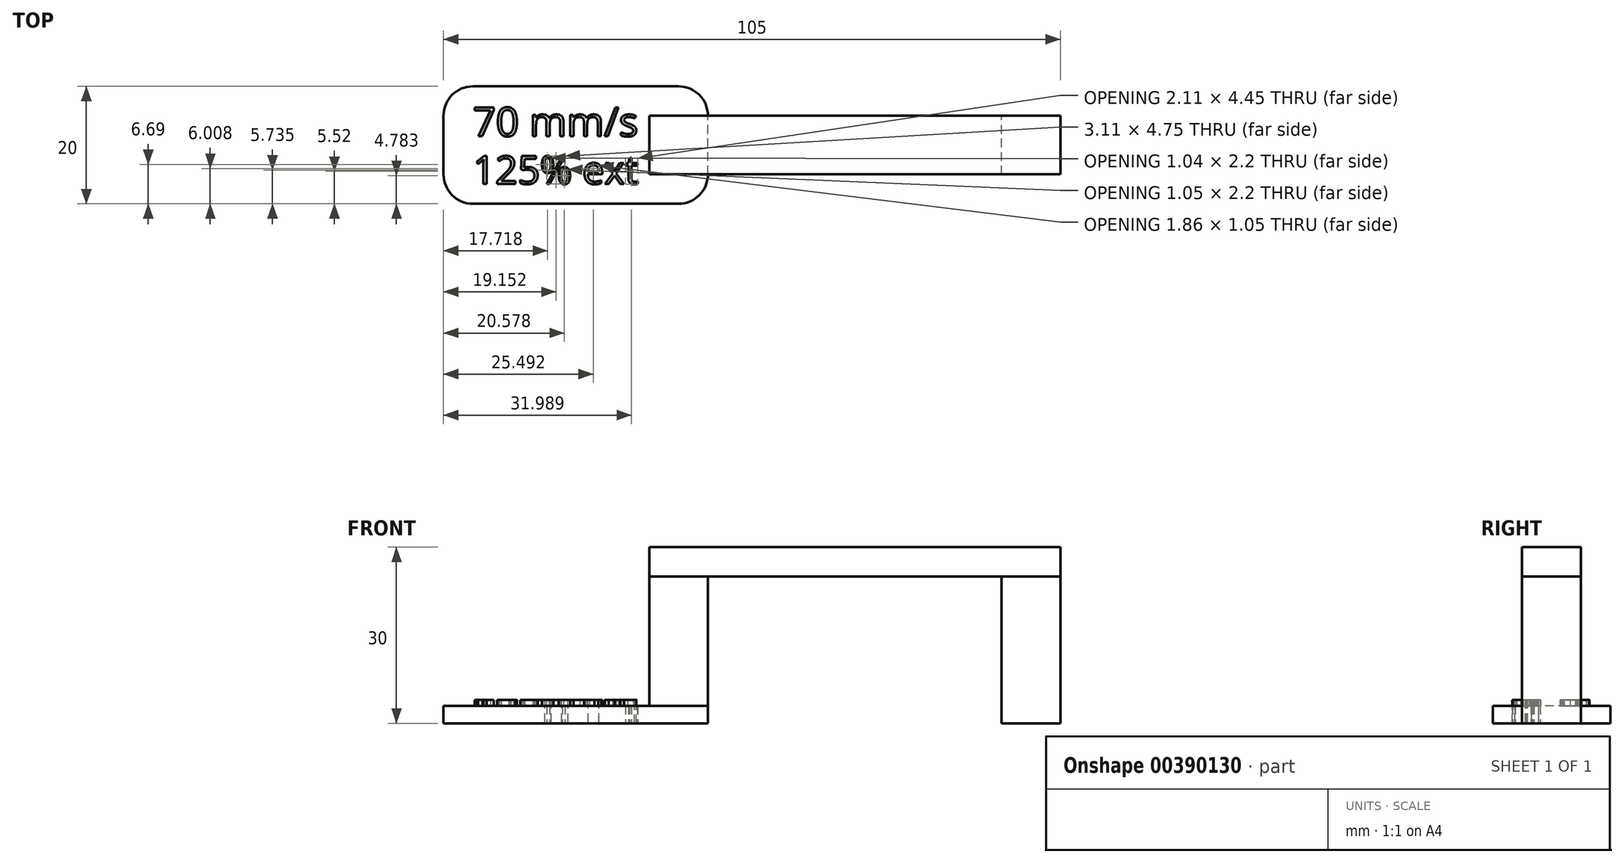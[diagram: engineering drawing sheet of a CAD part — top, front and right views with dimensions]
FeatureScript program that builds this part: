
annotation { "Feature Type Name" : "Feature", "Feature Type Description" : "" }
export const myFeature = defineFeature(function(context is Context, id is Id, definition is map)
    precondition{}
    {
        {
            var Q0;
            Q0=qCreatedBy(makeId("Top.planeOp"),FACE);
            var sketch = newSketch(context, id + "F0", { "sketchPlane" : qUnion([Q0])});
            skLineSegment(sketch, "E0.bottom", {"start": v(-25, -5) * mm, "end": v(25, -5) * mm});
            skLineSegment(sketch, "E0.top", {"start": v(-25, 5) * mm, "end": v(25, 5) * mm});
            skLineSegment(sketch, "E0.left", {"start": v(-25, -5) * mm, "end": v(-25, 5) * mm});
            skLineSegment(sketch, "E0.right", {"start": v(25, -5) * mm, "end": v(25, 5) * mm});
            skLineSegment(sketch, "E1.bottom", {"start": v(25, -5) * mm, "end": v(35, -5) * mm});
            skLineSegment(sketch, "E1.top", {"start": v(25, 5) * mm, "end": v(35, 5) * mm});
            skLineSegment(sketch, "E1.right", {"start": v(35, -5) * mm, "end": v(35, 5) * mm});
            skPoint(sketch, "E2.oppositeSnap0", {"position": v(0, -5) * mm});
            skLineSegment(sketch, "E2.bottom", {"start": v(-25, 5) * mm, "end": v(-35, 5) * mm});
            skLineSegment(sketch, "E2.top", {"start": v(-25, -5) * mm, "end": v(-35, -5) * mm});
            skLineSegment(sketch, "E2.left", {"start": v(-25, 5) * mm, "end": v(-25, -5) * mm});
            skLineSegment(sketch, "E2.right", {"start": v(-35, 5) * mm, "end": v(-35, -5) * mm});
            skLineSegment(sketch, "E3", {"start": v(-25, 5) * mm, "end": v(-25, 5) * mm});
            skLineSegment(sketch, "E4", {"start": v(-30, 10) * mm, "end": v(-65, 10) * mm});
            skLineSegment(sketch, "E5", {"start": v(-70, 5) * mm, "end": v(-70, -5) * mm});
            skLineSegment(sketch, "E6", {"start": v(-65, -10) * mm, "end": v(-30, -10) * mm});
            skLineSegment(sketch, "E7", {"start": v(-25, -5) * mm, "end": v(-25, -5) * mm});
            skLineSegment(sketch, "E8", {"start": v(-35, 0) * mm, "end": v(25, 0) * mm, "construction": true});
            skPoint(sketch, "E9.visualSharp", {"position": v(-70, -10) * mm});
            skArc(sketch, "E9.filletArc", {"start": v(-70, -5) * mm, "mid": v(-68.54, -8.54) * mm, "end": v(-65, -10) * mm});
            skPoint(sketch, "E10.visualSharp", {"position": v(-70, 10) * mm});
            skArc(sketch, "E10.filletArc", {"start": v(-65, 10) * mm, "mid": v(-68.54, 8.54) * mm, "end": v(-70, 5) * mm});
            skPoint(sketch, "E11.visualSharp", {"position": v(-25, -10) * mm});
            skArc(sketch, "E11.filletArc", {"start": v(-30, -10) * mm, "mid": v(-26.46, -8.54) * mm, "end": v(-25, -5) * mm});
            skPoint(sketch, "E12.visualSharp", {"position": v(-25, 10) * mm});
            skArc(sketch, "E12.filletArc", {"start": v(-25, 5) * mm, "mid": v(-26.46, 8.54) * mm, "end": v(-30, 10) * mm});
            skText(sketch, "E13", { "text": "70 mm/s", "fontName": "OpenSans-Regular.ttf"});
            skText(sketch, "E14", { "text": "125% ext", "fontName": "OpenSans-Regular.ttf"});
            const initialGuessF0  = {"E13": [-0.065, 0.00149, 1, 0, 0.00493], "E14": [-0.065, -0.00664, 1, 0, 0.00479]};
            skSetInitialGuess(sketch, initialGuessF0);
            skSolve(sketch);
        }
        {
            var Q0;
            Q0=makeQuery(id+"F0.imprint","IMPRINT",FACE,{"disambiguationData":[TD([[makeQuery(id+"F0.imprint","IMPRINT",EDGE,{"derivedFrom":sQuery(id+"F0.wireOp",EDGE,"E1.bottom")}),1.0]])]});
            var Q1;
            Q1=makeQuery(id+"F0.imprint","IMPRINT",FACE,{"disambiguationData":[TD([[makeQuery(id+"F0.imprint","IMPRINT",EDGE,{"derivedFrom":sQuery(id+"F0.wireOp",EDGE,"E2.bottom")}),1.0]])]});
            extrude(context, id + "F1", {"entities" : qUnion([Q0, Q1]), "depth" : 25 * mm});
        }
        {
            var Q0;
            Q0=makeQuery(id+"F0.imprint","IMPRINT",FACE,{"disambiguationData":[TD([[makeQuery(id+"F0.imprint","IMPRINT",EDGE,{"derivedFrom":sQuery(id+"F0.wireOp",EDGE,"E0.bottom")}),1.0]])]});
            var Q1;
            Q1=makeQuery(id+"F0.imprint","IMPRINT",FACE,{"disambiguationData":[TD([[makeQuery(id+"F0.imprint","IMPRINT",EDGE,{"derivedFrom":sQuery(id+"F0.wireOp",EDGE,"E2.bottom")}),1.0]])]});
            var Q2;
            Q2=makeQuery(id+"F0.imprint","IMPRINT",FACE,{"disambiguationData":[TD([[makeQuery(id+"F0.imprint","IMPRINT",EDGE,{"derivedFrom":sQuery(id+"F0.wireOp",EDGE,"E1.bottom")}),1.0]])]});
            var Q3;
            Q3=makeQuery(id+"F1.opExtrude","CAP_FACE",FACE,{"disambiguationData":[OSD([sQuery(id+"F0.wireOp",EDGE,"E1.bottom"),sQuery(id+"F0.wireOp",EDGE,"E1.top"),sQuery(id+"F0.wireOp",EDGE,"E0.right"),sQuery(id+"F0.wireOp",EDGE,"E1.right")])],"isStart":false});
            extrude(context, id + "F2", {"entities" : qUnion([Q0, Q1, Q2]), "depth" : 30 * mm, "hasSecondDirection" : true, "secondDirectionBound" : SecondDirectionBoundingType.UP_TO_SURFACE, "secondDirectionOppositeDirection" : false, "secondDirectionBoundEntityFace" : qUnion([Q3]), "secondDirectionDepth" : 25 * mm});
        }
        {
            var Q0;
            Q0=makeQuery(id+"F0.imprint","IMPRINT",FACE,{"disambiguationData":[TD([[makeQuery(id+"F0.imprint","IMPRINT",EDGE,{"derivedFrom":sQuery(id+"F0.wireOp",EDGE,"E2.bottom")}),1.0]])]});
            var Q1;
            Q1=makeQuery(id+"F0.imprint","IMPRINT",FACE,{"disambiguationData":[TD([[makeQuery(id+"F0.imprint","IMPRINT",EDGE,{"derivedFrom":sQuery(id+"F0.wireOp",EDGE,"E2.bottom")}),-1.0]])]});
            var Q2;
            Q2=makeQuery(id+"F0.imprint","IMPRINT",FACE,{"disambiguationData":[TD([[makeQuery(id+"F0.imprint","IMPRINT",EDGE,{"derivedFrom":sQuery(id+"F0.wireOp",EDGE,"E13.sketch_text.stroke-0")}),-1.0]])]});
            var Q3;
            Q3=makeQuery(id+"F0.imprint","IMPRINT",FACE,{"disambiguationData":[TD([[makeQuery(id+"F0.imprint","IMPRINT",EDGE,{"derivedFrom":sQuery(id+"F0.wireOp",EDGE,"E13.sketch_text.stroke-36")}),1.0]])]});
            var Q4;
            Q4=makeQuery(id+"F0.imprint","IMPRINT",FACE,{"disambiguationData":[TD([[makeQuery(id+"F0.imprint","IMPRINT",EDGE,{"derivedFrom":sQuery(id+"F0.wireOp",EDGE,"E13.sketch_text.stroke-28")}),-1.0]])]});
            var Q5;
            Q5=makeQuery(id+"F0.imprint","IMPRINT",FACE,{"disambiguationData":[TD([[makeQuery(id+"F0.imprint","IMPRINT",EDGE,{"derivedFrom":sQuery(id+"F0.wireOp",EDGE,"E14.sketch_text.stroke-89")}),1.0]])]});
            var Q6;
            Q6=makeQuery(id+"F0.imprint","IMPRINT",FACE,{"disambiguationData":[TD([[makeQuery(id+"F0.imprint","IMPRINT",EDGE,{"derivedFrom":sQuery(id+"F0.wireOp",EDGE,"E14.sketch_text.stroke-55")}),-1.0]])]});
            var Q7;
            Q7=makeQuery(id+"F0.imprint","IMPRINT",FACE,{"disambiguationData":[TD([[makeQuery(id+"F0.imprint","IMPRINT",EDGE,{"derivedFrom":sQuery(id+"F0.wireOp",EDGE,"E14.sketch_text.stroke-94")}),-1.0]])]});
            var Q8;
            Q8=makeQuery(id+"F0.imprint","IMPRINT",FACE,{"disambiguationData":[TD([[makeQuery(id+"F0.imprint","IMPRINT",EDGE,{"derivedFrom":sQuery(id+"F0.wireOp",EDGE,"E14.sketch_text.stroke-41")}),-1.0]])]});
            var Q9;
            Q9=makeQuery(id+"F0.imprint","IMPRINT",FACE,{"disambiguationData":[TD([[makeQuery(id+"F0.imprint","IMPRINT",EDGE,{"derivedFrom":sQuery(id+"F0.wireOp",EDGE,"E14.sketch_text.stroke-25")}),-1.0]])]});
            var Q10;
            Q10=makeQuery(id+"F0.imprint","IMPRINT",FACE,{"disambiguationData":[TD([[makeQuery(id+"F0.imprint","IMPRINT",EDGE,{"derivedFrom":sQuery(id+"F0.wireOp",EDGE,"E14.sketch_text.stroke-9")}),-1.0]])]});
            var Q11;
            Q11=makeQuery(id+"F0.imprint","IMPRINT",FACE,{"disambiguationData":[TD([[makeQuery(id+"F0.imprint","IMPRINT",EDGE,{"derivedFrom":sQuery(id+"F0.wireOp",EDGE,"E14.sketch_text.stroke-106")}),-1.0]])]});
            var Q12;
            Q12=makeQuery(id+"F0.imprint","IMPRINT",FACE,{"disambiguationData":[TD([[makeQuery(id+"F0.imprint","IMPRINT",EDGE,{"derivedFrom":sQuery(id+"F0.wireOp",EDGE,"E13.sketch_text.stroke-44")}),-1.0]])]});
            var Q13;
            Q13=makeQuery(id+"F0.imprint","IMPRINT",FACE,{"disambiguationData":[TD([[makeQuery(id+"F0.imprint","IMPRINT",EDGE,{"derivedFrom":sQuery(id+"F0.wireOp",EDGE,"E13.sketch_text.stroke-72")}),-1.0]])]});
            var Q14;
            Q14=makeQuery(id+"F0.imprint","IMPRINT",FACE,{"disambiguationData":[TD([[makeQuery(id+"F0.imprint","IMPRINT",EDGE,{"derivedFrom":sQuery(id+"F0.wireOp",EDGE,"E13.sketch_text.stroke-100")}),-1.0]])]});
            var Q15;
            Q15=makeQuery(id+"F0.imprint","IMPRINT",FACE,{"disambiguationData":[TD([[makeQuery(id+"F0.imprint","IMPRINT",EDGE,{"derivedFrom":sQuery(id+"F0.wireOp",EDGE,"E13.sketch_text.stroke-104")}),-1.0]])]});
            var Q16;
            Q16=makeQuery(id+"F0.imprint","IMPRINT",FACE,{"disambiguationData":[TD([[makeQuery(id+"F0.imprint","IMPRINT",EDGE,{"derivedFrom":sQuery(id+"F0.wireOp",EDGE,"E14.sketch_text.stroke-0")}),-1.0]])]});
            var Q17;
            Q17=makeQuery(id+"F0.imprint","IMPRINT",FACE,{"disambiguationData":[TD([[makeQuery(id+"F0.imprint","IMPRINT",EDGE,{"derivedFrom":sQuery(id+"F0.wireOp",EDGE,"E14.sketch_text.stroke-17")}),1.0]])]});
            var Q18;
            Q18=makeQuery(id+"F0.imprint","IMPRINT",FACE,{"disambiguationData":[TD([[makeQuery(id+"F0.imprint","IMPRINT",EDGE,{"derivedFrom":sQuery(id+"F0.wireOp",EDGE,"E14.sketch_text.stroke-33")}),1.0]])]});
            var Q19;
            Q19=makeQuery(id+"F0.imprint","IMPRINT",FACE,{"disambiguationData":[TD([[makeQuery(id+"F0.imprint","IMPRINT",EDGE,{"derivedFrom":sQuery(id+"F0.wireOp",EDGE,"E14.sketch_text.stroke-41")}),1.0]])]});
            var Q20;
            Q20=makeQuery(id+"F0.imprint","IMPRINT",FACE,{"disambiguationData":[TD([[makeQuery(id+"F0.imprint","IMPRINT",EDGE,{"derivedFrom":sQuery(id+"F0.wireOp",EDGE,"E14.sketch_text.stroke-55")}),1.0]])]});
            var Q21;
            Q21=makeQuery(id+"F0.imprint","IMPRINT",FACE,{"disambiguationData":[TD([[makeQuery(id+"F0.imprint","IMPRINT",EDGE,{"derivedFrom":sQuery(id+"F0.wireOp",EDGE,"E14.sketch_text.stroke-71")}),-1.0]])]});
            var Q22;
            Q22=makeQuery(id+"F0.imprint","IMPRINT",FACE,{"disambiguationData":[TD([[makeQuery(id+"F0.imprint","IMPRINT",EDGE,{"derivedFrom":sQuery(id+"F0.wireOp",EDGE,"E14.sketch_text.stroke-75")}),-1.0]])]});
            var Q23;
            Q23=makeQuery(id+"F0.imprint","IMPRINT",FACE,{"disambiguationData":[TD([[makeQuery(id+"F0.imprint","IMPRINT",EDGE,{"derivedFrom":sQuery(id+"F0.wireOp",EDGE,"E13.sketch_text.stroke-27")}),1.0]])]});
            var Q24;
            Q24=makeQuery(id+"F0.imprint","IMPRINT",FACE,{"disambiguationData":[TD([[makeQuery(id+"F0.imprint","IMPRINT",EDGE,{"derivedFrom":sQuery(id+"F0.wireOp",EDGE,"E13.sketch_text.stroke-91")}),-1.0]])]});
            var Q25;
            Q25=makeQuery(id+"F0.imprint","IMPRINT",FACE,{"disambiguationData":[TD([[makeQuery(id+"F0.imprint","IMPRINT",EDGE,{"derivedFrom":sQuery(id+"F0.wireOp",EDGE,"E13.sketch_text.stroke-15")}),1.0]])]});
            var Q26;
            Q26=makeQuery(id+"F0.imprint","IMPRINT",FACE,{"disambiguationData":[TD([[makeQuery(id+"F0.imprint","IMPRINT",EDGE,{"derivedFrom":sQuery(id+"F0.wireOp",EDGE,"E13.sketch_text.stroke-7")}),-1.0]])]});
            var Q27;
            Q27=makeQuery(id+"F0.imprint","IMPRINT",FACE,{"disambiguationData":[TD([[makeQuery(id+"F0.imprint","IMPRINT",EDGE,{"derivedFrom":sQuery(id+"F0.wireOp",EDGE,"E13.sketch_text.stroke-79")}),-1.0]])]});
            var Q28;
            Q28=makeQuery(id+"F0.imprint","IMPRINT",FACE,{"disambiguationData":[TD([[makeQuery(id+"F0.imprint","IMPRINT",EDGE,{"derivedFrom":sQuery(id+"F0.wireOp",EDGE,"E13.sketch_text.stroke-17")}),1.0]])]});
            var Q29;
            Q29=makeQuery(id+"F0.imprint","IMPRINT",FACE,{"disambiguationData":[TD([[makeQuery(id+"F0.imprint","IMPRINT",EDGE,{"derivedFrom":sQuery(id+"F0.wireOp",EDGE,"E13.sketch_text.stroke-9")}),-1.0]])]});
            var Q30;
            Q30=makeQuery(id+"F0.imprint","IMPRINT",FACE,{"disambiguationData":[TD([[makeQuery(id+"F0.imprint","IMPRINT",EDGE,{"derivedFrom":sQuery(id+"F0.wireOp",EDGE,"E13.sketch_text.stroke-81")}),-1.0]])]});
            extrude(context, id + "F3", {"entities" : qUnion([Q0, Q1, Q2, Q3, Q4, Q5, Q6, Q7, Q8, Q9, Q10, Q11, Q12, Q13, Q14, Q15, Q16, Q17, Q18, Q19, Q20, Q21, Q22, Q23, Q24, Q25, Q26, Q27, Q28, Q29, Q30]), "operationType" : NewBodyOperationType.ADD, "depth" : 3 * mm});
        }
        {
            var Q0;
            Q0=makeQuery(id+"F0.imprint","IMPRINT",FACE,{"disambiguationData":[TD([[makeQuery(id+"F0.imprint","IMPRINT",EDGE,{"derivedFrom":sQuery(id+"F0.wireOp",EDGE,"E14.sketch_text.stroke-0")}),-1.0]])]});
            var Q1;
            Q1=makeQuery(id+"F0.imprint","IMPRINT",FACE,{"disambiguationData":[TD([[makeQuery(id+"F0.imprint","IMPRINT",EDGE,{"derivedFrom":sQuery(id+"F0.wireOp",EDGE,"E14.sketch_text.stroke-9")}),-1.0]])]});
            var Q2;
            Q2=makeQuery(id+"F0.imprint","IMPRINT",FACE,{"disambiguationData":[TD([[makeQuery(id+"F0.imprint","IMPRINT",EDGE,{"derivedFrom":sQuery(id+"F0.wireOp",EDGE,"E14.sketch_text.stroke-25")}),-1.0]])]});
            var Q3;
            Q3=makeQuery(id+"F0.imprint","IMPRINT",FACE,{"disambiguationData":[TD([[makeQuery(id+"F0.imprint","IMPRINT",EDGE,{"derivedFrom":sQuery(id+"F0.wireOp",EDGE,"E14.sketch_text.stroke-41")}),-1.0]])]});
            var Q4;
            Q4=makeQuery(id+"F0.imprint","IMPRINT",FACE,{"disambiguationData":[TD([[makeQuery(id+"F0.imprint","IMPRINT",EDGE,{"derivedFrom":sQuery(id+"F0.wireOp",EDGE,"E14.sketch_text.stroke-71")}),-1.0]])]});
            var Q5;
            Q5=makeQuery(id+"F0.imprint","IMPRINT",FACE,{"disambiguationData":[TD([[makeQuery(id+"F0.imprint","IMPRINT",EDGE,{"derivedFrom":sQuery(id+"F0.wireOp",EDGE,"E14.sketch_text.stroke-55")}),-1.0]])]});
            var Q6;
            Q6=makeQuery(id+"F0.imprint","IMPRINT",FACE,{"disambiguationData":[TD([[makeQuery(id+"F0.imprint","IMPRINT",EDGE,{"derivedFrom":sQuery(id+"F0.wireOp",EDGE,"E14.sketch_text.stroke-75")}),-1.0]])]});
            var Q7;
            Q7=makeQuery(id+"F0.imprint","IMPRINT",FACE,{"disambiguationData":[TD([[makeQuery(id+"F0.imprint","IMPRINT",EDGE,{"derivedFrom":sQuery(id+"F0.wireOp",EDGE,"E14.sketch_text.stroke-94")}),-1.0]])]});
            var Q8;
            Q8=makeQuery(id+"F0.imprint","IMPRINT",FACE,{"disambiguationData":[TD([[makeQuery(id+"F0.imprint","IMPRINT",EDGE,{"derivedFrom":sQuery(id+"F0.wireOp",EDGE,"E14.sketch_text.stroke-106")}),-1.0]])]});
            var Q9;
            Q9=makeQuery(id+"F0.imprint","IMPRINT",FACE,{"disambiguationData":[TD([[makeQuery(id+"F0.imprint","IMPRINT",EDGE,{"derivedFrom":sQuery(id+"F0.wireOp",EDGE,"E13.sketch_text.stroke-28")}),-1.0]])]});
            var Q10;
            Q10=makeQuery(id+"F0.imprint","IMPRINT",FACE,{"disambiguationData":[TD([[makeQuery(id+"F0.imprint","IMPRINT",EDGE,{"derivedFrom":sQuery(id+"F0.wireOp",EDGE,"E13.sketch_text.stroke-0")}),-1.0]])]});
            var Q11;
            Q11=makeQuery(id+"F0.imprint","IMPRINT",FACE,{"disambiguationData":[TD([[makeQuery(id+"F0.imprint","IMPRINT",EDGE,{"derivedFrom":sQuery(id+"F0.wireOp",EDGE,"E13.sketch_text.stroke-44")}),-1.0]])]});
            var Q12;
            Q12=makeQuery(id+"F0.imprint","IMPRINT",FACE,{"disambiguationData":[TD([[makeQuery(id+"F0.imprint","IMPRINT",EDGE,{"derivedFrom":sQuery(id+"F0.wireOp",EDGE,"E13.sketch_text.stroke-72")}),-1.0]])]});
            var Q13;
            Q13=makeQuery(id+"F0.imprint","IMPRINT",FACE,{"disambiguationData":[TD([[makeQuery(id+"F0.imprint","IMPRINT",EDGE,{"derivedFrom":sQuery(id+"F0.wireOp",EDGE,"E13.sketch_text.stroke-100")}),-1.0]])]});
            var Q14;
            Q14=makeQuery(id+"F0.imprint","IMPRINT",FACE,{"disambiguationData":[TD([[makeQuery(id+"F0.imprint","IMPRINT",EDGE,{"derivedFrom":sQuery(id+"F0.wireOp",EDGE,"E13.sketch_text.stroke-104")}),-1.0]])]});
            var Q15;
            Q15=makeQuery(id+"F0.imprint","IMPRINT",FACE,{"disambiguationData":[TD([[makeQuery(id+"F0.imprint","IMPRINT",EDGE,{"derivedFrom":sQuery(id+"F0.wireOp",EDGE,"E13.sketch_text.stroke-91")}),-1.0]])]});
            var Q16;
            Q16=makeQuery(id+"F0.imprint","IMPRINT",FACE,{"disambiguationData":[TD([[makeQuery(id+"F0.imprint","IMPRINT",EDGE,{"derivedFrom":sQuery(id+"F0.wireOp",EDGE,"E13.sketch_text.stroke-7")}),-1.0]])]});
            var Q17;
            Q17=makeQuery(id+"F0.imprint","IMPRINT",FACE,{"disambiguationData":[TD([[makeQuery(id+"F0.imprint","IMPRINT",EDGE,{"derivedFrom":sQuery(id+"F0.wireOp",EDGE,"E13.sketch_text.stroke-79")}),-1.0]])]});
            var Q18;
            Q18=makeQuery(id+"F0.imprint","IMPRINT",FACE,{"disambiguationData":[TD([[makeQuery(id+"F0.imprint","IMPRINT",EDGE,{"derivedFrom":sQuery(id+"F0.wireOp",EDGE,"E13.sketch_text.stroke-9")}),-1.0]])]});
            var Q19;
            Q19=makeQuery(id+"F0.imprint","IMPRINT",FACE,{"disambiguationData":[TD([[makeQuery(id+"F0.imprint","IMPRINT",EDGE,{"derivedFrom":sQuery(id+"F0.wireOp",EDGE,"E13.sketch_text.stroke-81")}),-1.0]])]});
            extrude(context, id + "F4", {"entities" : qUnion([Q0, Q1, Q2, Q3, Q4, Q5, Q6, Q7, Q8, Q9, Q10, Q11, Q12, Q13, Q14, Q15, Q16, Q17, Q18, Q19]), "operationType" : NewBodyOperationType.ADD, "depth" : 4 * mm});
        }
    });
